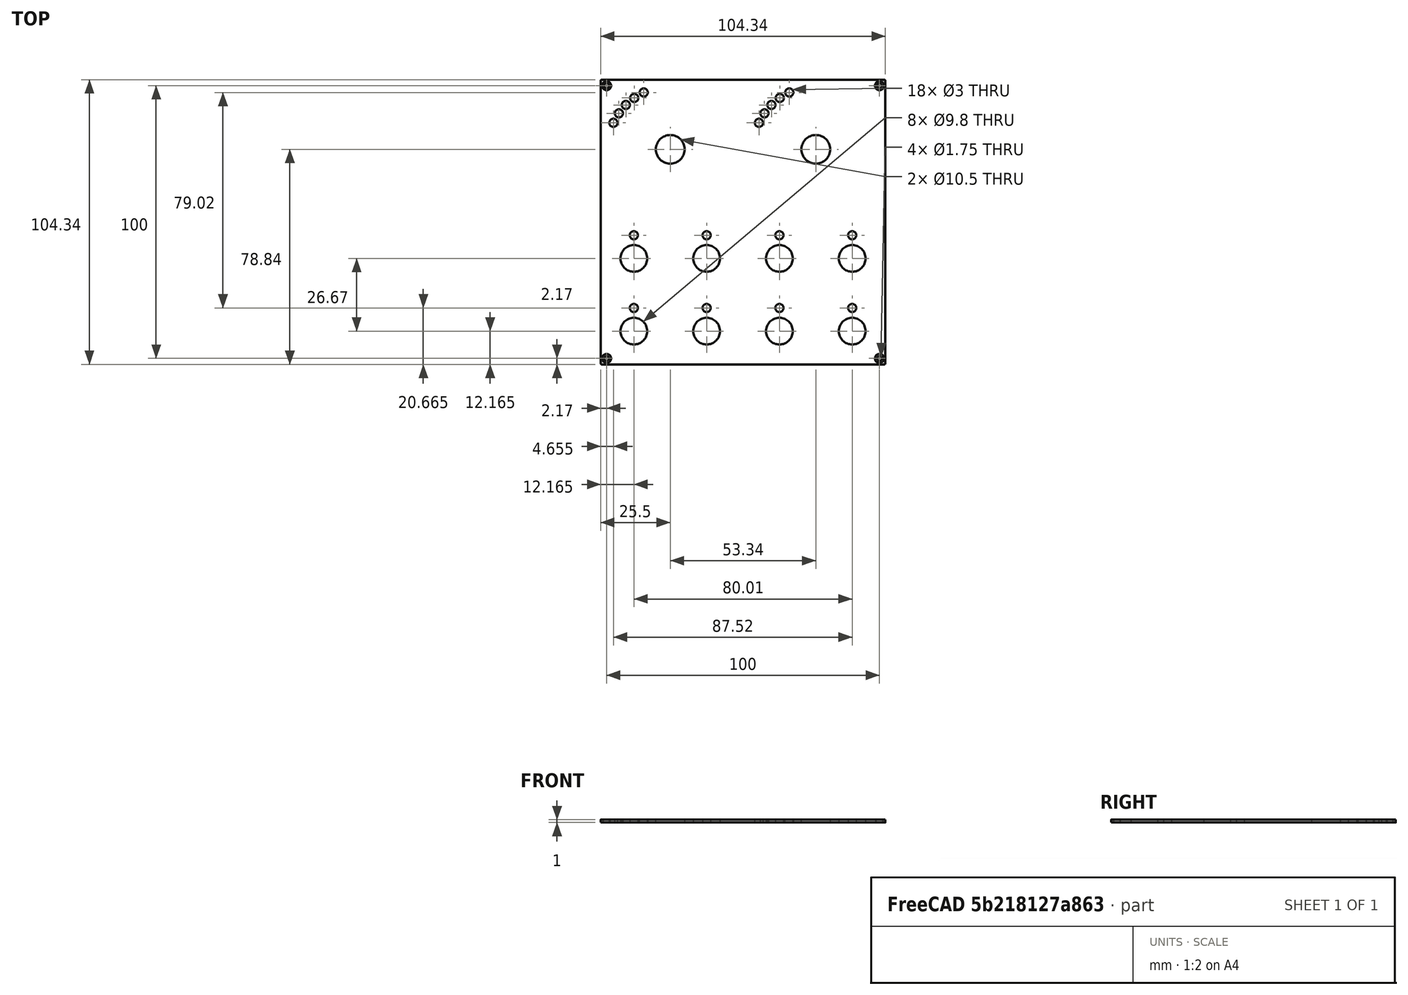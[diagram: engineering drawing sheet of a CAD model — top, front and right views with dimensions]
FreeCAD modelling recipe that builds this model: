
FCSTD DOCUMENT  (FreeCAD 0.21R33771 (Git))
Label: FRONTPANEL-SHEET-TEK2
License: All rights reserved
LicenseURL: https://en.wikipedia.org/wiki/All_rights_reserved
objects: TechDraw::DrawViewBalloon×16, TechDraw::DrawViewDimension×11, Sketcher::SketchObject×7, TechDraw::DrawViewPart×5, TechDraw::DrawHatch×5, PartDesign::Hole×3, TechDraw::DrawViewAnnotation×3, TechDraw::DrawSVGTemplate×2, PartDesign::Pocket×2, PartDesign::Body×2, TechDraw::DrawPage×2, Spreadsheet::Sheet×1, PartDesign::Pad×1, PartDesign::FeatureBase×1, TechDraw::DrawComplexSection×1
note: 37 computed .brp shape members not serialized (recipe doc carries the construction recipe); baked Part::Feature solids carry a one-line shape summary decoded from their .brp

FEATURE [TechDraw::DrawSVGTemplate] Template
  EditableTexts = COLOR=Anodized matte black - RAL code: 9004; CreationDate=2024/05/14; E.G.APPROVED=APPROVED; FC-Scale=1:1; FC-Title=TEK2 - frontpanel; IntechStudioLtd.=Intech Studio Ltd.; MATERIAL=Aluminum 5052-H32; REV=03; STANDARD=ISO 2768 - m
  Height = 297
  Orientation = 1
  Template = <userpath>/Desktop/A3_LandscapeTD_MODIFIED.svg
  Width = 420
FEATURE [Spreadsheet::Sheet] Spreadsheet  label="dim"
  cells = A1='panel_length; B1(panel_length)=104.35; A2='panel_thickness; B2(panel_thickness)=1; A3='panel_radius; B3(panel_radius)==(104.35 - 103.6) / 2; A5='corner_drill_dist; B5(corner_drill_dist)=100; A6='corner_drill_dia; B6(corner_drill_dia)=1.75; A7='corner_drill_countersink; B7(corner_drill_countersink)=3.3; A9='undercut_width; B9(undercut_width)=1; A10='undercut_length; B10(undercut_length)=90; A11='undercut_offset; B11(undercut_offset)=1; A12='undercut_depth; B12(undercut_depth)=0.8; A14='ui_raster; B14(ui_raster)=26.67; A16='light_drill_dia; B16(light_drill_dia)=3; D16='old 2.9; A17='light_bore_dia; B17(light_bore_dia)=3.45; C17='check; D17='old 3.30; E17='DEPRICATED; A18='light_bore_depth; B18(light_bore_depth)=0.4; C18='check; D18='old 0.40; E18='DEPRICATED; A20='pot_drill_dia; B20(pot_drill_dia)=9.8; C20='check; D20='old 6.20; A21='pot_led_dist; B21(pot_led_dist)=8.5; B22=0; A23='but_drill_dia; B23(but_drill_dia)=9.8; A24='but_led_dist; B24(but_led_dist)=8.5; A26='fad_cutout_width; B26(fad_cutout_width)=2.1; C26='check; D26='old 1.50; A27='fad_cutout_length; B27(fad_cutout_length)=36; A28='fad_led_dist; B28(fad_led_dist)=25; A30='enc_drill_dia; B30(enc_drill_dia)=9.8; C30='check; D30='old 6.20; A31='enc_led_dist; B31(enc_led_dist)=8.5; A33='longfad_cutout_width; B33(longfad_cutout_width)=2.1; A34='longfad_cutout_length; B34(longfad_cutout_length)=66; A36='panel_chamfer; B36(panel_chamfer)=0.2; C36='UPDATE DRAWING
FEATURE [Sketcher::SketchObject] Sketch025
  FullyConstrained = true
  MapMode = 5
  Support = -> [XY_Plane011]
  expr: Constraints[49] = <<dim>>.light_drill_dia
  sketch-geometry (28):
    g0: Circle CenterX=-26.67 CenterY=26.67 CenterZ=0 NormalX=0 NormalY=0 NormalZ=1 AngleXU=0 Radius=5.25
    g1: Circle CenterX=26.67 CenterY=26.67 CenterZ=0 NormalX=0 NormalY=0 NormalZ=1 AngleXU=0 Radius=5.25
    g2: LineSegment StartX=-26.67 StartY=26.67 StartZ=0 EndX=0 EndY=26.67 EndZ=0
    g3: LineSegment StartX=0 StartY=26.67 StartZ=0 EndX=0 EndY=0 EndZ=0
    g4: LineSegment StartX=26.67 StartY=26.67 StartZ=0 EndX=0 EndY=26.67 EndZ=0
    g5: Circle CenterX=-26.67 CenterY=26.67 CenterZ=0 NormalX=0 NormalY=0 NormalZ=1 AngleXU=0 Radius=23
    g6: Circle CenterX=26.67 CenterY=26.67 CenterZ=0 NormalX=0 NormalY=0 NormalZ=1 AngleXU=0 Radius=23
    g7: Circle CenterX=-47.5151 CenterY=36.3902 CenterZ=0 NormalX=0 NormalY=0 NormalZ=1 AngleXU=0 Radius=1.5
    g8: Circle CenterX=-45.5105 CenterY=39.8623 CenterZ=0 NormalX=0 NormalY=0 NormalZ=1 AngleXU=0 Radius=1.5
    g9: Circle CenterX=-42.9335 CenterY=42.9335 CenterZ=0 NormalX=0 NormalY=0 NormalZ=1 AngleXU=0 Radius=1.5
    g10: Circle CenterX=-39.8623 CenterY=45.5105 CenterZ=0 NormalX=0 NormalY=0 NormalZ=1 AngleXU=0 Radius=1.5
    g11: Circle CenterX=-36.3902 CenterY=47.5151 CenterZ=0 NormalX=0 NormalY=0 NormalZ=1 AngleXU=0 Radius=1.5
    g12: Circle CenterX=5.82492 CenterY=36.3902 CenterZ=0 NormalX=0 NormalY=0 NormalZ=1 AngleXU=0 Radius=1.5
    g13: Circle CenterX=7.8295 CenterY=39.8623 CenterZ=0 NormalX=0 NormalY=0 NormalZ=1 AngleXU=0 Radius=1.5
    g14: Circle CenterX=10.4065 CenterY=42.9335 CenterZ=0 NormalX=0 NormalY=0 NormalZ=1 AngleXU=0 Radius=1.5
    g15: Circle CenterX=13.4777 CenterY=45.5105 CenterZ=0 NormalX=0 NormalY=0 NormalZ=1 AngleXU=0 Radius=1.5
    g16: Circle CenterX=16.9498 CenterY=47.5151 CenterZ=0 NormalX=0 NormalY=0 NormalZ=1 AngleXU=0 Radius=1.5
    g17: LineSegment StartX=-47.5151 StartY=36.3902 StartZ=0 EndX=5.82492 EndY=36.3902 EndZ=0
    g18: LineSegment StartX=-45.5105 StartY=39.8623 StartZ=0 EndX=7.8295 EndY=39.8623 EndZ=0
    g19: LineSegment StartX=-42.9335 StartY=42.9335 StartZ=0 EndX=10.4065 EndY=42.9335 EndZ=0
    g20: LineSegment StartX=-39.8623 StartY=45.5105 StartZ=0 EndX=13.4777 EndY=45.5105 EndZ=0
    g21: LineSegment StartX=-36.3902 StartY=47.5151 StartZ=0 EndX=16.9498 EndY=47.5151 EndZ=0
    g22: LineSegment StartX=5.82492 StartY=36.3902 StartZ=0 EndX=26.67 EndY=26.67 EndZ=0
    g23: LineSegment StartX=16.9498 StartY=47.5151 StartZ=0 EndX=26.67 EndY=26.67 EndZ=0
    g24: LineSegment StartX=5.82492 StartY=36.3902 StartZ=0 EndX=7.8295 EndY=39.8623 EndZ=0
    g25: LineSegment StartX=7.8295 StartY=39.8623 StartZ=0 EndX=10.4065 EndY=42.9335 EndZ=0
    g26: LineSegment StartX=13.4777 StartY=45.5105 StartZ=0 EndX=10.4065 EndY=42.9335 EndZ=0
    g27: LineSegment StartX=16.9498 StartY=47.5151 StartZ=0 EndX=13.4777 EndY=45.5105 EndZ=0
  constraints (69):
    c: Coincident(g2,g0)
    c: PointOnObject(g2,g-2)
    c: Coincident(g2,g3)
    c: Coincident(g3,g-1)
    c: Coincident(g4,g1)
    c: Coincident(g4,g2)
    c: Equal(g3,g2)
    c: Equal(g2,g4)
    c: Horizontal(g2)
    c: Horizontal(g4)
    c: DistanceY(g3,g3) = 26.67
    c: Equal(g0,g1)
    c: Coincident(g5,g0)
    c: Coincident(g6,g1)
    c: Equal(g6,g5)
    c: PointOnObject(g7,g5)
    c: PointOnObject(g8,g5)
    c: PointOnObject(g9,g5)
    c: PointOnObject(g10,g5)
    c: PointOnObject(g11,g5)
    c: PointOnObject(g12,g6)
    c: PointOnObject(g13,g6)
    c: PointOnObject(g14,g6)
    c: PointOnObject(g15,g6)
    c: PointOnObject(g16,g6)
    c: Equal(g7,g8)
    c: Equal(g8,g9)
    c: Equal(g9,g10)
    c: Equal(g10,g11)
    c: Equal(g11,g12)
    c: Equal(g12,g13)
    c: Equal(g13,g14)
    c: Equal(g14,g15)
    c: Equal(g15,g16)
    c: Coincident(g17,g7)
    c: Coincident(g17,g12)
    c: Coincident(g18,g8)
    c: Coincident(g18,g13)
    c: Horizontal(g18)
    c: Coincident(g19,g9)
    c: Coincident(g19,g14)
    c: Horizontal(g19)
    c: Coincident(g20,g10)
    c: Coincident(g20,g15)
    c: Horizontal(g20)
    c: Coincident(g21,g11)
    c: Horizontal(g21)
    c: Coincident(g21,g16)
    c: Horizontal(g17)
    c: Diameter(g12) = 3
    c: Coincident(g22,g12)
    c: Coincident(g22,g1)
    c: Coincident(g23,g16)
    c: Coincident(g23,g1)
    c: Angle(g22,g4) = 0.436332
    c: Angle(g-2,g23) = 0.436332
    c: Coincident(g24,g12)
    c: Coincident(g24,g13)
    c: Coincident(g25,g13)
    c: Coincident(g26,g15)
    c: Coincident(g26,g25)
    c: Coincident(g27,g16)
    c: Coincident(g27,g15)
    c: Coincident(g25,g14)
    c: Equal(g24,g25)
    c: Equal(g25,g26)
    c: Equal(g26,g27)
    c: Radius(g6) = 23
    c: Diameter(g1) = 10.5
FEATURE [Sketcher::SketchObject] Sketch024
  FullyConstrained = true
  MapMode = 5
  Support = -> [XY_Plane011]
  expr: Constraints[42] = <<dim>>.but_led_dist
  sketch-geometry (17):
    g0: Circle CenterX=-40.005 CenterY=-4.835 CenterZ=0 NormalX=0 NormalY=0 NormalZ=1 AngleXU=0 Radius=2
    g1: Circle CenterX=-13.335 CenterY=-4.835 CenterZ=0 NormalX=0 NormalY=0 NormalZ=1 AngleXU=0 Radius=2
    g2: LineSegment StartX=-40.005 StartY=-4.835 StartZ=0 EndX=-13.335 EndY=-4.835 EndZ=0
    g3: Circle CenterX=13.335 CenterY=-4.835 CenterZ=0 NormalX=0 NormalY=0 NormalZ=1 AngleXU=0 Radius=2
    g4: LineSegment StartX=-13.335 StartY=-4.835 StartZ=0 EndX=13.335 EndY=-4.835 EndZ=0
    g5: Circle CenterX=40.005 CenterY=-4.835 CenterZ=0 NormalX=0 NormalY=0 NormalZ=1 AngleXU=0 Radius=2
    g6: LineSegment StartX=13.335 StartY=-4.835 StartZ=0 EndX=40.005 EndY=-4.835 EndZ=0
    g7: Circle CenterX=-40.005 CenterY=-31.505 CenterZ=0 NormalX=0 NormalY=0 NormalZ=1 AngleXU=0 Radius=2
    g8: LineSegment StartX=-40.005 StartY=-4.835 StartZ=0 EndX=-40.005 EndY=-31.505 EndZ=0
    g9: Circle CenterX=-13.335 CenterY=-31.505 CenterZ=0 NormalX=0 NormalY=0 NormalZ=1 AngleXU=0 Radius=2
    g10: LineSegment StartX=-40.005 StartY=-31.505 StartZ=0 EndX=-13.335 EndY=-31.505 EndZ=0
    g11: Circle CenterX=13.335 CenterY=-31.505 CenterZ=0 NormalX=0 NormalY=0 NormalZ=1 AngleXU=0 Radius=2
    g12: LineSegment StartX=-13.335 StartY=-31.505 StartZ=0 EndX=13.335 EndY=-31.505 EndZ=0
    g13: Circle CenterX=40.005 CenterY=-31.505 CenterZ=0 NormalX=0 NormalY=0 NormalZ=1 AngleXU=0 Radius=2
    g14: LineSegment StartX=13.335 StartY=-31.505 StartZ=0 EndX=40.005 EndY=-31.505 EndZ=0
    g15: LineSegment StartX=-13.335 StartY=-4.835 StartZ=0 EndX=-1.8e-15 EndY=8.5 EndZ=0
    g16: LineSegment StartX=-1.8e-15 StartY=8.5 StartZ=0 EndX=13.335 EndY=-4.835 EndZ=0
  constraints (43):
    c: Diameter(g0) = 4
    c: Coincident(g0,g2)
    c: Coincident(g1,g2)
    c: Coincident(g1,g4)
    c: Coincident(g3,g4)
    c: Coincident(g3,g6)
    c: Coincident(g5,g6)
    c: Coincident(g0,g8)
    c: Coincident(g7,g8)
    c: Coincident(g7,g10)
    c: Coincident(g9,g10)
    c: Coincident(g9,g12)
    c: Coincident(g11,g12)
    c: Coincident(g11,g14)
    c: Coincident(g13,g14)
    c: Horizontal(g4)
    c: Horizontal(g2)
    c: Horizontal(g6)
    c: Horizontal(g10)
    c: Horizontal(g12)
    c: Horizontal(g14)
    c: Vertical(g8)
    c: Equal(g8,g2)
    c: Equal(g2,g10)
    c: Equal(g10,g12)
    c: Equal(g12,g4)
    c: Equal(g4,g6)
    c: Equal(g6,g14)
    c: DistanceX(g4,g4) = 26.67
    c: Equal(g7,g9)
    c: Equal(g9,g11)
    c: Equal(g11,g13)
    c: Equal(g13,g5)
    c: Equal(g5,g3)
    c: Equal(g3,g1)
    c: Equal(g1,g0)
    c: Coincident(g15,g1)
    c: PointOnObject(g15,g-2)
    c: Coincident(g15,g16)
    c: Coincident(g16,g3)
    c: Equal(g16,g15)
    c: Perpendicular(g15,g16)
    c: DistanceY(g-1,g15) = 8.5
FEATURE [Sketcher::SketchObject] Sketch023
  FullyConstrained = true
  MapMode = 5
  Support = -> [XY_Plane011]
  sketch-geometry (17):
    g0: Circle CenterX=-40.005 CenterY=-13.335 CenterZ=0 NormalX=0 NormalY=0 NormalZ=1 AngleXU=0 Radius=2
    g1: Circle CenterX=-13.335 CenterY=-13.335 CenterZ=0 NormalX=0 NormalY=0 NormalZ=1 AngleXU=0 Radius=2
    g2: LineSegment StartX=-40.005 StartY=-13.335 StartZ=0 EndX=-13.335 EndY=-13.335 EndZ=0
    g3: Circle CenterX=13.335 CenterY=-13.335 CenterZ=0 NormalX=0 NormalY=0 NormalZ=1 AngleXU=0 Radius=2
    g4: LineSegment StartX=-13.335 StartY=-13.335 StartZ=0 EndX=13.335 EndY=-13.335 EndZ=0
    g5: Circle CenterX=40.005 CenterY=-13.335 CenterZ=0 NormalX=0 NormalY=0 NormalZ=1 AngleXU=0 Radius=2
    g6: LineSegment StartX=13.335 StartY=-13.335 StartZ=0 EndX=40.005 EndY=-13.335 EndZ=0
    g7: Circle CenterX=-40.005 CenterY=-40.005 CenterZ=0 NormalX=0 NormalY=0 NormalZ=1 AngleXU=0 Radius=2
    g8: LineSegment StartX=-40.005 StartY=-13.335 StartZ=0 EndX=-40.005 EndY=-40.005 EndZ=0
    g9: Circle CenterX=-13.335 CenterY=-40.005 CenterZ=0 NormalX=0 NormalY=0 NormalZ=1 AngleXU=0 Radius=2
    g10: LineSegment StartX=-40.005 StartY=-40.005 StartZ=0 EndX=-13.335 EndY=-40.005 EndZ=0
    g11: Circle CenterX=13.335 CenterY=-40.005 CenterZ=0 NormalX=0 NormalY=0 NormalZ=1 AngleXU=0 Radius=2
    g12: LineSegment StartX=-13.335 StartY=-40.005 StartZ=0 EndX=13.335 EndY=-40.005 EndZ=0
    g13: Circle CenterX=40.005 CenterY=-40.005 CenterZ=0 NormalX=0 NormalY=0 NormalZ=1 AngleXU=0 Radius=2
    g14: LineSegment StartX=13.335 StartY=-40.005 StartZ=0 EndX=40.005 EndY=-40.005 EndZ=0
    g15: LineSegment StartX=0 StartY=0 StartZ=0 EndX=13.335 EndY=-13.335 EndZ=0
    g16: LineSegment StartX=0 StartY=0 StartZ=0 EndX=-13.335 EndY=-13.335 EndZ=0
  constraints (42):
    c: Diameter(g0) = 4
    c: Coincident(g0,g2)
    c: Coincident(g1,g2)
    c: Coincident(g1,g4)
    c: Coincident(g3,g4)
    c: Coincident(g3,g6)
    c: Coincident(g5,g6)
    c: Coincident(g0,g8)
    c: Coincident(g7,g8)
    c: Coincident(g7,g10)
    c: Coincident(g9,g10)
    c: Coincident(g9,g12)
    c: Coincident(g11,g12)
    c: Coincident(g11,g14)
    c: Coincident(g13,g14)
    c: Coincident(g-1,g16)
    c: Coincident(g16,g1)
    c: Coincident(g15,g3)
    c: Horizontal(g4)
    c: Horizontal(g2)
    c: Horizontal(g6)
    c: Horizontal(g10)
    c: Horizontal(g12)
    c: Horizontal(g14)
    c: Vertical(g8)
    c: Equal(g8,g2)
    c: Equal(g2,g10)
    c: Equal(g10,g12)
    c: Equal(g12,g4)
    c: Equal(g4,g6)
    c: Equal(g6,g14)
    c: DistanceX(g4,g4) = 26.67
    c: Equal(g16,g15)
    c: Coincident(g15,g16)
    c: Perpendicular(g15,g16)
    c: Equal(g7,g9)
    c: Equal(g9,g11)
    c: Equal(g11,g13)
    c: Equal(g13,g5)
    c: Equal(g5,g3)
    c: Equal(g3,g1)
    c: Equal(g1,g0)
FEATURE [Sketcher::SketchObject] Sketch001
  FullyConstrained = true
  MapMode = 5
  Support = -> [XY_Plane]
  expr: Constraints[13] = <<dim>>.corner_drill_dist
  sketch-geometry (9):
    g0: LineSegment StartX=-50 StartY=50 StartZ=0 EndX=-50 EndY=-50 EndZ=0
    g1: LineSegment StartX=-50 StartY=-50 StartZ=0 EndX=50 EndY=-50 EndZ=0
    g2: LineSegment StartX=50 StartY=-50 StartZ=0 EndX=50 EndY=50 EndZ=0
    g3: LineSegment StartX=50 StartY=50 StartZ=0 EndX=-50 EndY=50 EndZ=0
    g4: Circle CenterX=0 CenterY=0 CenterZ=0 NormalX=0 NormalY=0 NormalZ=1 AngleXU=0 Radius=70.7107
    g5: Circle CenterX=-50 CenterY=50 CenterZ=0 NormalX=0 NormalY=0 NormalZ=1 AngleXU=0 Radius=0.5
    g6: Circle CenterX=50 CenterY=50 CenterZ=0 NormalX=0 NormalY=0 NormalZ=1 AngleXU=0 Radius=0.5
    g7: Circle CenterX=50 CenterY=-50 CenterZ=0 NormalX=0 NormalY=0 NormalZ=1 AngleXU=0 Radius=0.5
    g8: Circle CenterX=-50 CenterY=-50 CenterZ=0 NormalX=0 NormalY=0 NormalZ=1 AngleXU=0 Radius=0.5
  constraints (22):
    c: Coincident(g0,g1)
    c: Coincident(g1,g2)
    c: Coincident(g2,g3)
    c: Coincident(g3,g0)
    c: Equal(g0,g1)
    c: Equal(g0,g2)
    c: Equal(g0,g3)
    c: PointOnObject(g0,g4)
    c: PointOnObject(g1,g4)
    c: PointOnObject(g2,g4)
    c: PointOnObject(g3,g4)
    c: Coincident(g4,g-1)
    c: Horizontal(g3)
    c: DistanceX(g3,g3) = 100
    c: Coincident(g5,g0)
    c: Coincident(g6,g2)
    c: Coincident(g7,g1)
    c: Coincident(g8,g0)
    c: Diameter(g8) = 1
    c: Equal(g8,g7)
    c: Equal(g8,g6)
    c: Equal(g8,g5)
FEATURE [Sketcher::SketchObject] Sketch002
  AttachmentOffset = pos=(0,0,-4.8) rot=(0,0,1;0rad)
  FullyConstrained = true
  MapMode = 5
  Placement = pos=(0,0,-4.8) rot=(0,0,1;0rad)
  Support = -> [XY_Plane]
  expr: .AttachmentOffset.Base.z = -<<dim>>.undercut_depth - 4
  expr: Constraints[91] = <<dim>>.undercut_length
  expr: Constraints[92] = <<dim>>.undercut_width
  expr: Constraints[93] = <<dim>>.panel_length / 2 - <<dim>>.undercut_offset - <<dim>>.undercut_width / 2
  sketch-geometry (40):
    g0: LineSegment StartX=-45 StartY=50.175 StartZ=0 EndX=45 EndY=50.175 EndZ=0
    g1: LineSegment StartX=-45 StartY=51.175 StartZ=0 EndX=45 EndY=51.175 EndZ=0
    g2: LineSegment StartX=-50.675 StartY=45 StartZ=0 EndX=0 EndY=0 EndZ=0
    g3: LineSegment StartX=0 StartY=0 StartZ=0 EndX=-50.675 EndY=-45 EndZ=0
    g4: LineSegment StartX=0 StartY=0 StartZ=0 EndX=-45 EndY=50.675 EndZ=0
    g5: LineSegment StartX=45 StartY=50.675 StartZ=0 EndX=0 EndY=0 EndZ=0
    g6: LineSegment StartX=0 StartY=0 StartZ=0 EndX=50.675 EndY=45 EndZ=0
    g7: LineSegment StartX=50.675 StartY=-45 StartZ=0 EndX=0 EndY=0 EndZ=0
    g8: LineSegment StartX=0 StartY=0 StartZ=0 EndX=45 EndY=-50.675 EndZ=0
    g9: LineSegment StartX=0 StartY=0 StartZ=0 EndX=-45 EndY=-50.675 EndZ=0
    g10: ArcOfCircle CenterX=45 CenterY=50.675 CenterZ=0 NormalX=0 NormalY=0 NormalZ=1 AngleXU=0 Radius=0.5 StartAngle=4.71239 EndAngle=6.28319
    g11: ArcOfCircle CenterX=45 CenterY=50.675 CenterZ=0 NormalX=0 NormalY=0 NormalZ=1 AngleXU=0 Radius=0.5 StartAngle=0 EndAngle=1.5708
    g12: LineSegment StartX=45 StartY=50.675 StartZ=0 EndX=45.5 EndY=50.675 EndZ=0
    g13: ArcOfCircle CenterX=-45 CenterY=50.675 CenterZ=0 NormalX=0 NormalY=0 NormalZ=1 AngleXU=0 Radius=0.5 StartAngle=3.14159 EndAngle=4.71239
    g14: ArcOfCircle CenterX=-45 CenterY=50.675 CenterZ=0 NormalX=0 NormalY=0 NormalZ=1 AngleXU=0 Radius=0.5 StartAngle=1.5708 EndAngle=3.14159
    g15: LineSegment StartX=-45.5 StartY=50.675 StartZ=0 EndX=-45 EndY=50.675 EndZ=0
    g16: LineSegment StartX=-45 StartY=-51.175 StartZ=0 EndX=45 EndY=-51.175 EndZ=0
    g17: LineSegment StartX=-45 StartY=-50.175 StartZ=0 EndX=45 EndY=-50.175 EndZ=0
    g18: ArcOfCircle CenterX=45 CenterY=-50.675 CenterZ=0 NormalX=0 NormalY=0 NormalZ=1 AngleXU=0 Radius=0.5 StartAngle=4.71239 EndAngle=6.28319
    g19: ArcOfCircle CenterX=45 CenterY=-50.675 CenterZ=0 NormalX=0 NormalY=0 NormalZ=1 AngleXU=0 Radius=0.5 StartAngle=0 EndAngle=1.5708
    g20: LineSegment StartX=45 StartY=-50.675 StartZ=0 EndX=45.5 EndY=-50.675 EndZ=0
    g21: ArcOfCircle CenterX=-45 CenterY=-50.675 CenterZ=0 NormalX=0 NormalY=0 NormalZ=1 AngleXU=0 Radius=0.5 StartAngle=3.14159 EndAngle=4.71239
    g22: ArcOfCircle CenterX=-45 CenterY=-50.675 CenterZ=0 NormalX=0 NormalY=0 NormalZ=1 AngleXU=0 Radius=0.5 StartAngle=1.5708 EndAngle=3.14159
    g23: LineSegment StartX=-45.5 StartY=-50.675 StartZ=0 EndX=-45 EndY=-50.675 EndZ=0
    g24: LineSegment StartX=51.175 StartY=-45 StartZ=0 EndX=51.175 EndY=45 EndZ=0
    g25: LineSegment StartX=50.175 StartY=-45 StartZ=0 EndX=50.175 EndY=45 EndZ=0
    g26: ArcOfCircle CenterX=50.675 CenterY=45 CenterZ=0 NormalX=0 NormalY=0 NormalZ=1 AngleXU=0 Radius=0.5 StartAngle=3.8e-15 EndAngle=1.5708
    g27: ArcOfCircle CenterX=50.675 CenterY=45 CenterZ=0 NormalX=0 NormalY=0 NormalZ=1 AngleXU=0 Radius=0.5 StartAngle=1.5708 EndAngle=3.14159
    g28: LineSegment StartX=50.675 StartY=45 StartZ=0 EndX=50.675 EndY=45.5 EndZ=0
    g29: ArcOfCircle CenterX=50.675 CenterY=-45 CenterZ=0 NormalX=0 NormalY=0 NormalZ=1 AngleXU=0 Radius=0.5 StartAngle=4.71239 EndAngle=6.28319
    g30: ArcOfCircle CenterX=50.675 CenterY=-45 CenterZ=0 NormalX=0 NormalY=0 NormalZ=1 AngleXU=0 Radius=0.5 StartAngle=3.14159 EndAngle=4.71239
    g31: LineSegment StartX=50.675 StartY=-45.5 StartZ=0 EndX=50.675 EndY=-45 EndZ=0
    g32: LineSegment StartX=-50.175 StartY=-45 StartZ=0 EndX=-50.175 EndY=45 EndZ=0
    g33: LineSegment StartX=-51.175 StartY=-45 StartZ=0 EndX=-51.175 EndY=45 EndZ=0
    g34: ArcOfCircle CenterX=-50.675 CenterY=45 CenterZ=0 NormalX=0 NormalY=0 NormalZ=1 AngleXU=0 Radius=0.5 StartAngle=1.4e-15 EndAngle=1.5708
    g35: ArcOfCircle CenterX=-50.675 CenterY=45 CenterZ=0 NormalX=0 NormalY=0 NormalZ=1 AngleXU=0 Radius=0.5 StartAngle=1.5708 EndAngle=3.14159
    g36: LineSegment StartX=-50.675 StartY=45 StartZ=0 EndX=-50.675 EndY=45.5 EndZ=0
    g37: ArcOfCircle CenterX=-50.675 CenterY=-45 CenterZ=0 NormalX=0 NormalY=0 NormalZ=1 AngleXU=0 Radius=0.5 StartAngle=4.71239 EndAngle=6.28319
    g38: ArcOfCircle CenterX=-50.675 CenterY=-45 CenterZ=0 NormalX=0 NormalY=0 NormalZ=1 AngleXU=0 Radius=0.5 StartAngle=3.14159 EndAngle=4.71239
    g39: LineSegment StartX=-50.675 StartY=-45.5 StartZ=0 EndX=-50.675 EndY=-45 EndZ=0
  constraints (96):
    c: Horizontal(g0)
    c: Coincident(g2,g-1)
    c: Coincident(g2,g3)
    c: Coincident(g-1,g4)
    c: Coincident(g5,g-1)
    c: Coincident(g5,g6)
    c: Coincident(g7,g-1)
    c: Coincident(g7,g8)
    c: Coincident(g-1,g9)
    c: Equal(g5,g6)
    c: Equal(g6,g8)
    c: Equal(g8,g7)
    c: Equal(g7,g9)
    c: Equal(g9,g3)
    c: Equal(g3,g2)
    c: Equal(g2,g4)
    c: Coincident(g10,g5)
    c: Coincident(g11,g10)
    c: Coincident(g11,g10)
    c: Tangent(g11,g1) = 1.5708
    c: Tangent(g10,g0) = -1.5708
    c: Coincident(g12,g10)
    c: Coincident(g12,g10)
    c: Horizontal(g12)
    c: Coincident(g13,g4)
    c: Coincident(g14,g13)
    c: Coincident(g14,g13)
    c: Tangent(g14,g1) = 1.5708
    c: Tangent(g13,g0) = -1.5708
    c: Coincident(g15,g13)
    c: Coincident(g15,g13)
    c: Horizontal(g15)
    c: Horizontal(g1)
    c: Horizontal(g16)
    c: Coincident(g19,g18)
    c: Coincident(g19,g18)
    c: Tangent(g19,g17) = 1.5708
    c: Tangent(g18,g16) = -1.5708
    c: Coincident(g20,g18)
    c: Coincident(g20,g18)
    c: Horizontal(g20)
    c: Coincident(g22,g21)
    c: Coincident(g22,g21)
    c: Tangent(g22,g17) = 1.5708
    c: Tangent(g21,g16) = -1.5708
    c: Coincident(g23,g21)
    c: Coincident(g23,g21)
    c: Horizontal(g23)
    c: Horizontal(g17)
    c: Coincident(g21,g9)
    c: Coincident(g8,g18)
    c: Equal(g22,g14)
    c: Equal(g17,g1)
    c: Coincident(g27,g26)
    c: Coincident(g27,g26)
    c: Tangent(g27,g25) = 1.5708
    c: Tangent(g26,g24) = -1.5708
    c: Coincident(g28,g26)
    c: Coincident(g28,g26)
    c: Coincident(g30,g29)
    c: Coincident(g30,g29)
    c: Tangent(g30,g25) = 1.5708
    c: Tangent(g29,g24) = -1.5708
    c: Coincident(g31,g29)
    c: Coincident(g31,g29)
    c: Vertical(g31)
    c: Vertical(g28)
    c: Vertical(g25)
    c: Vertical(g24)
    c: Coincident(g35,g34)
    c: Coincident(g35,g34)
    c: Tangent(g35,g33) = 1.5708
    c: Tangent(g34,g32) = -1.5708
    c: Coincident(g36,g34)
    c: Coincident(g36,g34)
    c: Coincident(g38,g37)
    c: Coincident(g38,g37)
    c: Tangent(g38,g33) = 1.5708
    c: Tangent(g37,g32) = -1.5708
    c: Coincident(g39,g37)
    c: Coincident(g39,g37)
    c: Vertical(g39)
    c: Vertical(g36)
    c: Vertical(g33)
    c: Vertical(g32)
    c: Coincident(g6,g26)
    c: Coincident(g7,g29)
    c: Equal(g25,g0)
    c: Equal(g11,g27)
    c: Equal(g1,g33)
    c: Equal(g35,g11)
    c: DistanceX(g13,g10) = 90
    c: Diameter(g13) = 1
    c: DistanceY(g-1,g13) = 50.675
    c: Coincident(g2,g34)
    c: Coincident(g3,g37)
FEATURE [Sketcher::SketchObject] Sketch
  FullyConstrained = true
  MapMode = 5
  Support = -> [XY_Plane]
  expr: Constraints[12] = <<dim>>.panel_radius
  expr: Constraints[16] = <<dim>>.panel_length
  sketch-geometry (11):
    g0: LineSegment StartX=-51.8 StartY=52.175 StartZ=0 EndX=51.8 EndY=52.175 EndZ=0
    g1: LineSegment StartX=52.175 StartY=51.8 StartZ=0 EndX=52.175 EndY=-51.8 EndZ=0
    g2: LineSegment StartX=51.8 StartY=-52.175 StartZ=0 EndX=-51.8 EndY=-52.175 EndZ=0
    g3: LineSegment StartX=-52.175 StartY=-51.8 StartZ=0 EndX=-52.175 EndY=51.8 EndZ=0
    g4: ArcOfCircle CenterX=-51.8 CenterY=51.8 CenterZ=0 NormalX=0 NormalY=0 NormalZ=1 AngleXU=0 Radius=0.375 StartAngle=1.5708 EndAngle=3.14159
    g5: ArcOfCircle CenterX=51.8 CenterY=51.8 CenterZ=0 NormalX=0 NormalY=0 NormalZ=1 AngleXU=0 Radius=0.375 StartAngle=8.4e-15 EndAngle=1.5708
    g6: ArcOfCircle CenterX=51.8 CenterY=-51.8 CenterZ=0 NormalX=0 NormalY=0 NormalZ=1 AngleXU=0 Radius=0.375 StartAngle=4.71239 EndAngle=6.28319
    g7: ArcOfCircle CenterX=-51.8 CenterY=-51.8 CenterZ=0 NormalX=0 NormalY=0 NormalZ=1 AngleXU=0 Radius=0.375 StartAngle=3.14159 EndAngle=4.71239
    g8: LineSegment StartX=-51.8 StartY=51.8 StartZ=0 EndX=0 EndY=0 EndZ=0
    g9: LineSegment StartX=0 StartY=0 StartZ=0 EndX=51.8 EndY=51.8 EndZ=0
    g10: LineSegment StartX=0 StartY=0 StartZ=0 EndX=-51.8 EndY=-51.8 EndZ=0
  constraints (26):
    c: Horizontal(g0)
    c: Horizontal(g2)
    c: Vertical(g1)
    c: Vertical(g3)
    c: Tangent(g3,g4) = 1.5708
    c: Tangent(g0,g4) = 1.5708
    c: Tangent(g0,g5) = 1.5708
    c: Tangent(g1,g5) = 1.5708
    c: Tangent(g1,g6) = 1.5708
    c: Tangent(g2,g6) = 1.5708
    c: Tangent(g2,g7) = 1.5708
    c: Tangent(g3,g7) = 1.5708
    c: Radius(g4) = 0.375
    c: Equal(g4,g5)
    c: Equal(g4,g6)
    c: Equal(g4,g7)
    c: DistanceX(g3,g1) = 104.35
    c: Equal(g3,g0)
    c: Coincident(g8,g4)
    c: Coincident(g8,g-1)
    c: Coincident(g8,g9)
    c: Coincident(g9,g5)
    c: Coincident(g-1,g10)
    c: Coincident(g10,g7)
    c: Equal(g10,g8)
    c: Equal(g8,g9)
FEATURE [PartDesign::Pad] Pad  label="panel"
  AllowMultiFace = false
  Direction = (0,0,1)
  Length = 1
  Length2 = 100
  Profile = -> Sketch
  Reversed = true
  Type = 0
  expr: Length = <<dim>>.panel_thickness
FEATURE [PartDesign::Pocket] Pocket
  AllowMultiFace = false
  BaseFeature = -> Pad
  Direction = (0,0,-1)
  Length = 5
  Length2 = 100
  Profile = -> Sketch002
  Type = 1
FEATURE [PartDesign::Hole] Hole
  BaseFeature = -> Pocket
  CustomThreadClearance = 0
  Depth = 298.105
  DepthType = 1
  Diameter = 1.75
  DrillForDepth = false
  DrillPoint = 1
  DrillPointAngle = 118
  HoleCutCountersinkAngle = 90
  HoleCutCustomValues = false
  HoleCutDepth = 0
  HoleCutDiameter = 3.3
  HoleCutType = 2
  ModelThread = false
  Profile = -> Sketch001
  Tapered = false
  TaperedAngle = 90
  ThreadClass = 0
  ThreadDepth = 298.105
  ThreadDepthType = 0
  ThreadDirection = 0
  ThreadFit = 0
  ThreadSize = 0
  ThreadType = 0
  Threaded = false
  UseCustomThreadClearance = false
  expr: Diameter = <<dim>>.corner_drill_dia
  expr: HoleCutDiameter = <<dim>>.corner_drill_countersink
FEATURE [PartDesign::Body] Body  label="Base"
  Group = -> [Sketch,Pad,Sketch001,Sketch002,Pocket,Hole]
  Origin = -> Origin
  Tip = -> Hole
FEATURE [PartDesign::FeatureBase] Clone009
  BaseFeature = -> Body
FEATURE [PartDesign::Hole] Hole014  label="TEK2_ButtonHole"
  BaseFeature = -> Clone009
  CustomThreadClearance = 0
  Depth = 25
  DepthType = 0
  Diameter = 9.8
  DrillForDepth = false
  DrillPoint = 1
  DrillPointAngle = 118
  HoleCutCountersinkAngle = 90
  HoleCutCustomValues = false
  HoleCutDepth = 0
  HoleCutDiameter = 6.1
  HoleCutType = 0
  ModelThread = false
  Profile = -> Sketch023
  Tapered = false
  TaperedAngle = 90
  ThreadClass = 0
  ThreadDepth = 25
  ThreadDepthType = 0
  ThreadDirection = 0
  ThreadFit = 0
  ThreadSize = 0
  ThreadType = 0
  Threaded = false
  UseCustomThreadClearance = false
  expr: Diameter = <<dim>>.but_drill_dia
FEATURE [PartDesign::Hole] Hole015  label="TEK2_ButtonLight"
  BaseFeature = -> Hole014
  CustomThreadClearance = 0
  Depth = 25
  DepthType = 0
  Diameter = 3
  DrillForDepth = false
  DrillPoint = 1
  DrillPointAngle = 118
  HoleCutCountersinkAngle = 90
  HoleCutCustomValues = false
  HoleCutDepth = 0
  HoleCutDiameter = 6.1
  HoleCutType = 0
  ModelThread = false
  Profile = -> Sketch024
  Tapered = false
  TaperedAngle = 90
  ThreadClass = 0
  ThreadDepth = 25
  ThreadDepthType = 0
  ThreadDirection = 0
  ThreadFit = 0
  ThreadSize = 0
  ThreadType = 0
  Threaded = false
  UseCustomThreadClearance = false
  expr: Diameter = <<dim>>.light_drill_dia
FEATURE [PartDesign::Pocket] Pocket007  label="TEK2_TEK_Light"
  BaseFeature = -> Hole015
  Direction = (0,0,-1)
  Length = 5
  Length2 = 5
  Profile = -> Sketch025
  ReferenceAxis = -> Sketch025 [N_Axis]
  Type = 0
FEATURE [Sketcher::SketchObject] Sketch026
  ExternalGeometry = -> [Pocket007]
  FullyConstrained = true
  MapMode = 5
  Support = -> [XY_Plane011]
  sketch-geometry (1):
    g0: LineSegment StartX=-53.5 StartY=-50 StartZ=0 EndX=-46.5 EndY=-50 EndZ=0
  constraints (3):
    c: Horizontal(g0)
    c: Symmetric(g0,g0,g-3)
    c: DistanceX(g0,g0) = 7
FEATURE [PartDesign::Body] Body011  label="FRONTPANEL-SHEET-TEK2"
  BaseFeature = -> Body
  Group = -> [Clone009,Sketch023,Sketch024,Hole014,Hole015,Sketch025,Pocket007,Sketch026]
  Origin = -> Origin011
  Tip = -> Pocket007
FEATURE [TechDraw::DrawViewPart] View
  CoarseView = false
  Direction = (0,0,1)
  Focus = 100
  HardHidden = true
  IsoCount = 0
  IsoHidden = false
  IsoVisible = false
  LockPosition = false
  Perspective = false
  Rotation = 0
  ScaleType = 0
  ScrubCount = 0
  SeamHidden = false
  SeamVisible = true
  SmoothHidden = false
  SmoothVisible = true
  Source = -> [Body011]
  X = 98.8745
  XDirection = (1,0,0)
  Y = 197.053
FEATURE [TechDraw::DrawViewPart] View001
  CoarseView = false
  Direction = (-1,0,0)
  Focus = 100
  HardHidden = true
  IsoCount = 0
  IsoHidden = false
  IsoVisible = false
  LockPosition = false
  Perspective = false
  Rotation = 0
  ScaleType = 0
  ScrubCount = 0
  SeamHidden = false
  SeamVisible = true
  SmoothHidden = false
  SmoothVisible = true
  Source = -> [Body011]
  X = 195.483
  XDirection = (0,0,1)
  Y = 199.908
FEATURE [TechDraw::DrawViewPart] View002
  CoarseView = false
  Direction = (0,0,-1)
  Focus = 100
  HardHidden = true
  IsoCount = 0
  IsoHidden = false
  IsoVisible = false
  LockPosition = false
  Perspective = false
  Rotation = 0
  ScaleType = 0
  ScrubCount = 0
  SeamHidden = false
  SeamVisible = true
  SmoothHidden = false
  SmoothVisible = true
  Source = -> [Body011]
  X = 288.076
  XDirection = (-1,0,0)
  Y = 198.167
FEATURE [TechDraw::DrawViewDimension] Dimension
  AngleOverride = false
  Arbitrary = false
  ArbitraryTolerances = false
  EqualTolerance = false
  ExtensionAngle = 0
  FormatSpec = %.2w
  FormatSpecOverTolerance = %+.2w
  FormatSpecUnderTolerance = %+.2w
  Inverted = false
  LineAngle = 0
  LockPosition = false
  MeasureType = 1
  OverTolerance = 0
  References2D = -> [View]
  Rotation = 0
  ScaleType = 0
  TheoreticalExact = false
  Type = 2
  UnderTolerance = -0.2
  X = 61.7953
  Y = 1.34438
FEATURE [TechDraw::DrawViewDimension] Dimension001
  AngleOverride = false
  Arbitrary = false
  ArbitraryTolerances = false
  EqualTolerance = false
  ExtensionAngle = 0
  FormatSpec = %.2w
  FormatSpecOverTolerance = %+.2w
  FormatSpecUnderTolerance = %+.2w
  Inverted = false
  LineAngle = 0
  LockPosition = false
  MeasureType = 1
  OverTolerance = 0
  References2D = -> [View002]
  Rotation = 0
  ScaleType = 0
  TheoreticalExact = false
  Type = 1
  UnderTolerance = -0.2
  X = -6.41479
  Y = 69.0205
FEATURE [TechDraw::DrawViewBalloon] Balloon
  BubbleShape = 6
  EndType = 6
  EndTypeScale = 1
  KinkLength = 0
  LockPosition = false
  OriginX = 70.4982
  OriginY = 52.3109
  Rotation = 0
  ScaleType = 0
  ShapeScale = 1
  SourceView = -> Dimension
  Text = C
  TextWrapLen = -1
  X = 70.6756
  Y = 62.9547
FEATURE [TechDraw::DrawViewBalloon] Balloon001
  BubbleShape = 6
  EndType = 6
  EndTypeScale = 1
  KinkLength = -0.1
  LockPosition = false
  OriginX = -52.3226
  OriginY = 62.1981
  Rotation = 0
  ScaleType = 0
  ShapeScale = 1
  SourceView = -> Dimension001
  Text = B
  TextWrapLen = -1
  X = -60.7084
  Y = 62.1751
FEATURE [TechDraw::DrawViewBalloon] Balloon002
  BubbleShape = 6
  EndType = 0
  EndTypeScale = 1
  KinkLength = -0.1
  LockPosition = false
  OriginX = 0.5
  OriginY = 0
  Rotation = 0
  ScaleType = 0
  ShapeScale = 1
  SourceView = -> View001
  Text = ⏥|0,2
  TextWrapLen = -1
  X = 19.0698
  Y = 0.107397
FEATURE [TechDraw::DrawViewBalloon] Balloon003
  BubbleShape = 6
  EndType = 6
  EndTypeScale = 1
  KinkLength = -0.1
  LockPosition = false
  OriginX = 0.672888
  OriginY = 39.7383
  Rotation = 0
  ScaleType = 0
  ShapeScale = 1
  SourceView = -> View001
  Text = A
  TextWrapLen = -1
  X = 10.7916
  Y = 39.8457
FEATURE [TechDraw::DrawViewDimension] Dimension003
  AngleOverride = false
  Arbitrary = false
  ArbitraryTolerances = false
  EqualTolerance = true
  ExtensionAngle = 0
  FormatSpec = 2x ⌀%.2w
  FormatSpecOverTolerance = %+.2w
  FormatSpecUnderTolerance = %+.2w
  Inverted = false
  LineAngle = 0
  LockPosition = false
  MeasureType = 1
  OverTolerance = 0
  References2D = -> [View]
  Rotation = 0
  ScaleType = 0
  TheoreticalExact = false
  Type = 0
  UnderTolerance = 0
  X = -11.777
  Y = 72.7869
FEATURE [TechDraw::DrawViewBalloon] Balloon005
  BubbleShape = 6
  EndType = 6
  EndTypeScale = 1
  KinkLength = -0.1
  LockPosition = false
  OriginX = -31.9077
  OriginY = 67.4956
  Rotation = 0
  ScaleType = 0
  ShapeScale = 1
  SourceView = -> Dimension003
  Text = D
  TextWrapLen = -1
  X = -43.255
  Y = 67.5316
FEATURE [TechDraw::DrawViewBalloon] Balloon006
  BubbleShape = 6
  EndType = 7
  EndTypeScale = 1
  KinkLength = 0
  LockPosition = false
  OriginX = -8.73717
  OriginY = 64.838
  Rotation = 0
  ScaleType = 0
  ShapeScale = 1
  SourceView = -> Dimension003
  Text = ⌖|⌀ 0,15|A|B|C
  TextWrapLen = -1
  X = 9.10088
  Y = 61.9493
FEATURE [TechDraw::DrawViewDimension] Dimension004
  AngleOverride = false
  Arbitrary = false
  ArbitraryTolerances = false
  EqualTolerance = true
  ExtensionAngle = 0
  FormatSpec = 2x (⌀%.2w)
  FormatSpecOverTolerance = %+.2w
  FormatSpecUnderTolerance = %+.2w
  Inverted = false
  LineAngle = 0
  LockPosition = false
  MeasureType = 1
  OverTolerance = 0
  References2D = -> [View]
  Rotation = 0
  ScaleType = 0
  TheoreticalExact = false
  Type = 5
  UnderTolerance = 0
  X = 56.2833
  Y = 86.7255
FEATURE [TechDraw::DrawViewBalloon] Balloon007
  BubbleShape = 6
  EndType = 6
  EndTypeScale = 1
  KinkLength = 0
  LockPosition = false
  OriginX = 60.4502
  OriginY = 83.6888
  Rotation = 0
  ScaleType = 0
  ShapeScale = 1
  SourceView = -> Dimension004
  Text = ◎|⌀ 0,15|D
  TextWrapLen = -1
  X = 65.8595
  Y = 75.7457
FEATURE [TechDraw::DrawViewBalloon] Balloon008
  BubbleShape = 1
  EndType = 0
  EndTypeScale = 1
  KinkLength = -0.1
  LockPosition = false
  OriginX = -52.0652
  OriginY = 52.0652
  Rotation = 0
  ScaleType = 0
  ShapeScale = 1
  SourceView = -> View
  Text = 4x R0,38
  TextWrapLen = -1
  X = -75.4388
  Y = 68.3556
FEATURE [TechDraw::DrawViewDimension] Dimension006
  AngleOverride = false
  Arbitrary = false
  ArbitraryTolerances = false
  EqualTolerance = true
  ExtensionAngle = 0
  FormatSpec = 18x ⌀%.2w
  FormatSpecOverTolerance = %+.2w
  FormatSpecUnderTolerance = %+.2w
  Inverted = false
  LineAngle = 0
  LockPosition = false
  MeasureType = 1
  OverTolerance = 0.05
  References2D = -> [View002]
  Rotation = 0
  ScaleType = 0
  TheoreticalExact = false
  Type = 5
  UnderTolerance = -0.05
  X = 78.3293
  Y = -25.4917
FEATURE [TechDraw::DrawViewBalloon] Balloon010
  BubbleShape = 6
  EndType = 6
  EndTypeScale = 1
  KinkLength = 0
  LockPosition = false
  OriginX = 57.3508
  OriginY = -80.6381
  Rotation = 0
  ScaleType = 0
  ShapeScale = 1
  SourceView = -> Dimension006
  Text = ⌖|⌀ 0,15|A|B|C
  TextWrapLen = -1
  X = 91.3024
  Y = -36.3012
FEATURE [TechDraw::DrawComplexSection] ComplexSection  label="Section A - A"
  BaseView = -> View
  Caption = Section A-A
  CoarseView = false
  CutSurfaceDisplay = 2
  CuttingToolWireObject = -> Sketch026
  Direction = (1e-16,-1,0)
  FileGeomPattern = C:/Program Files/FreeCAD 0.21/data/Mod/TechDraw/PAT/FCPAT.pat
  FileHatchPattern = C:/Program Files/FreeCAD 0.21/data/Mod/TechDraw/Patterns/simple.svg
  Focus = 100
  FuseBeforeCut = false
  HardHidden = true
  HatchOffset = (0,0,0)
  HatchRotation = 0
  HatchScale = 1
  IsoCount = 0
  IsoHidden = false
  IsoVisible = false
  LockPosition = false
  NameGeomPattern = Gyémánt bevonatú
  Perspective = false
  ProjectionStrategy = 1
  Rotation = 0
  Scale = 10
  ScaleType = 2
  ScrubCount = 0
  SeamHidden = false
  SeamVisible = true
  SectionDirection = 4
  SectionNormal = (1e-16,-1,0)
  SectionOrigin = (0,0,0)
  SectionSymbol = A
  SmoothHidden = false
  SmoothVisible = true
  Source = -> [Body011]
  TrimAfterCut = false
  X = 89.9827
  XDirection = (1,1e-16,0)
  Y = 81.1022
FEATURE [TechDraw::DrawViewDimension] Dimension007
  AngleOverride = false
  Arbitrary = false
  ArbitraryTolerances = false
  EqualTolerance = true
  ExtensionAngle = 0
  FormatSpec = %.2w
  FormatSpecOverTolerance = %+.2w
  FormatSpecUnderTolerance = %+.2w
  Inverted = false
  LineAngle = 0
  LockPosition = false
  MeasureType = 1
  OverTolerance = 0
  References2D = -> [ComplexSection]
  Rotation = 0
  ScaleType = 0
  TheoreticalExact = false
  Type = 6
  UnderTolerance = 0
  X = -23.1172
  Y = 22.8219
FEATURE [TechDraw::DrawViewDimension] Dimension008
  AngleOverride = false
  Arbitrary = false
  ArbitraryTolerances = false
  EqualTolerance = true
  ExtensionAngle = 0
  FormatSpec = 4x ⌀%.2w
  FormatSpecOverTolerance = %+.2w
  FormatSpecUnderTolerance = %+.2w
  Inverted = false
  LineAngle = 0
  LockPosition = false
  MeasureType = 1
  OverTolerance = 0
  References2D = -> [ComplexSection]
  Rotation = 0
  ScaleType = 0
  TheoreticalExact = false
  Type = 1
  UnderTolerance = 0
  X = 25.5096
  Y = 18.3127
FEATURE [TechDraw::DrawViewDimension] Dimension009
  AngleOverride = false
  Arbitrary = false
  ArbitraryTolerances = false
  EqualTolerance = true
  ExtensionAngle = 0
  FormatSpec = 4x ⌀%.2w
  FormatSpecOverTolerance = %+.2w
  FormatSpecUnderTolerance = %+.2w
  Inverted = false
  LineAngle = 0
  LockPosition = false
  MeasureType = 1
  OverTolerance = 0.05
  References2D = -> [ComplexSection]
  Rotation = 0
  ScaleType = 0
  TheoreticalExact = false
  Type = 1
  UnderTolerance = -0.05
  X = 48.7908
  Y = -4.80347
FEATURE [TechDraw::DrawViewBalloon] Balloon012
  BubbleShape = 6
  EndType = 6
  EndTypeScale = 1
  KinkLength = 0
  LockPosition = false
  OriginX = 46.1954
  OriginY = -17.0078
  Rotation = 0
  ScaleType = 0
  ShapeScale = 1
  SourceView = -> Dimension009
  Text = ⌖|⌀ 0,15|A|B|C
  TextWrapLen = -1
  X = 60.7039
  Y = -15.6117
FEATURE [TechDraw::DrawViewDimension] Dimension010
  AngleOverride = false
  Arbitrary = false
  ArbitraryTolerances = false
  EqualTolerance = true
  ExtensionAngle = 0
  FormatSpec = (%.2w)
  FormatSpecOverTolerance = %+.2w
  FormatSpecUnderTolerance = %+.2w
  Inverted = false
  LineAngle = 0
  LockPosition = false
  MeasureType = 1
  OverTolerance = 0
  References2D = -> [ComplexSection]
  Rotation = 0
  ScaleType = 0
  TheoreticalExact = false
  Type = 2
  UnderTolerance = 0
  X = -36.693
  Y = 2
FEATURE [TechDraw::DrawViewAnnotation] Annotation
  Font = osifont
  LineSpace = 100
  LockPosition = false
  MaxWidth = -1
  Rotation = 0
  ScaleType = 0
  Text = 10:1
  TextSize = 4
  TextStyle = 0
  X = 86.742
  Y = 60.6655
FEATURE [TechDraw::DrawViewPart] View003
  CoarseView = false
  Direction = (0.57735,0.57735,0.57735)
  Focus = 100
  HardHidden = true
  IsoCount = 0
  IsoHidden = false
  IsoVisible = false
  LockPosition = false
  Perspective = false
  Rotation = 0
  Scale = 0.5
  ScaleType = 2
  ScrubCount = 0
  SeamHidden = false
  SeamVisible = true
  SmoothHidden = false
  SmoothVisible = true
  Source = -> [Body011]
  X = 386.287
  XDirection = (0.707107,0,-0.707107)
  Y = 119.321
FEATURE [TechDraw::DrawHatch] Hatch  label="HatchF1"
  HatchPattern = C:/Program Files/FreeCAD 0.21/data/Mod/TechDraw/Patterns/solid.svg
  Source = -> View003 [Face1]
FEATURE [TechDraw::DrawViewBalloon] Balloon013
  BubbleShape = 1
  EndType = 3
  EndTypeScale = 1
  KinkLength = -0.1
  LockPosition = false
  OriginX = -18.2151
  OriginY = -14.1288
  Rotation = 0
  ScaleType = 0
  ShapeScale = 1
  SourceView = -> View003
  TextWrapLen = -1
  X = -113.902
  Y = -52.9975
FEATURE [TechDraw::DrawViewAnnotation] Annotation001
  Font = osifont
  LineSpace = 100
  LockPosition = false
  MaxWidth = -1
  Rotation = 0
  ScaleType = 0
  Text = 1:2
  TextSize = 4
  TextStyle = 0
  X = 381.918
  Y = 90.0973
FEATURE [TechDraw::DrawViewAnnotation] Annotation002
  Font = osifont
  LineSpace = 100
  LockPosition = false
  MaxWidth = -1
  Rotation = 0
  ScaleType = 0
  Text = The mid of the datum plane A is preferred to be near | to the lower limit of the flatness tolerance zone. | It can be achieved with an additional bending step. | Aesthetical surfaces colored red on the view | No scratches, burrs or any kind of damage allowed! | Functional surfaces colored blue on the view (all which perpendicular to the aesthetical) | No burrs or other protruding material allowed!
  TextSize = 3
  TextStyle = 0
  X = 295.979
  Y = 101.86
FEATURE [TechDraw::DrawViewBalloon] Balloon015
  BubbleShape = 2
  EndType = 6
  EndTypeScale = 1
  KinkLength = 0
  LockPosition = false
  OriginX = -87.396
  OriginY = 27.2009
  Rotation = 0
  ScaleType = 0
  ShapeScale = 1
  SourceView = -> Annotation002
  Text = 3
  TextWrapLen = -1
  X = -96.2531
  Y = -1.91575
FEATURE [TechDraw::DrawViewDimension] Dimension011
  AngleOverride = false
  Arbitrary = false
  ArbitraryTolerances = false
  EqualTolerance = true
  ExtensionAngle = 0
  FormatSpec = 8× ⌀%.2w
  FormatSpecOverTolerance = %+.2w
  FormatSpecUnderTolerance = %+.2w
  Inverted = false
  LineAngle = 0
  LockPosition = false
  MeasureType = 1
  OverTolerance = 0
  References2D = -> [View002]
  Rotation = 0
  ScaleType = 0
  TheoreticalExact = false
  Type = 5
  UnderTolerance = 0
  X = 75.2192
  Y = -60.9974
FEATURE [TechDraw::DrawViewDimension] Dimension012
  AngleOverride = false
  Arbitrary = false
  ArbitraryTolerances = true
  EqualTolerance = false
  ExtensionAngle = 0
  FormatSpec = 8× ⌀%.2w
  FormatSpecOverTolerance = +0,15
  FormatSpecUnderTolerance = 0
  Inverted = false
  LineAngle = 0
  LockPosition = false
  MeasureType = 1
  OverTolerance = 0
  References2D = -> [View002]
  Rotation = 0
  ScaleType = 0
  TheoreticalExact = false
  Type = 5
  UnderTolerance = 0
  X = 72.4963
  Y = 8.04101
FEATURE [TechDraw::DrawViewBalloon] Balloon016
  BubbleShape = 6
  EndType = 6
  EndTypeScale = 1
  KinkLength = 0
  LockPosition = false
  OriginX = 79.0426
  OriginY = -7.7627
  Rotation = 0
  ScaleType = 0
  ShapeScale = 1
  SourceView = -> Dimension012
  Text = ⌖|⌀ 0,15|A|B|C
  TextWrapLen = -1
  X = 92.0678
  Y = -4.70292
FEATURE [TechDraw::DrawViewBalloon] Balloon017
  BubbleShape = 6
  EndType = 6
  EndTypeScale = 1
  KinkLength = 0
  LockPosition = false
  OriginX = 75.1018
  OriginY = -15.0221
  Rotation = 0
  ScaleType = 0
  ShapeScale = 1
  SourceView = -> Dimension012
  Text = ○|0,1
  TextWrapLen = -1
  X = 73.0244
  Y = -15.3225
FEATURE [TechDraw::DrawViewBalloon] Balloon018
  BubbleShape = 2
  EndType = 6
  EndTypeScale = 1
  KinkLength = 0
  LockPosition = false
  OriginX = 84.1342
  OriginY = 3.44725
  Rotation = 0
  ScaleType = 0
  ShapeScale = 1
  SourceView = -> Dimension012
  Text = 3
  TextWrapLen = -1
  X = 101.675
  Y = 5.46919
FEATURE [TechDraw::DrawViewBalloon] Balloon019
  BubbleShape = 1
  EndType = 0
  EndTypeScale = 1
  KinkLength = 0
  LockPosition = false
  OriginX = 0.785937
  OriginY = -33.6238
  Rotation = 0
  ScaleType = 0
  ShapeScale = 1
  SourceView = -> View001
  TextWrapLen = -1
  X = 22.117
  Y = -64.3933
FEATURE [TechDraw::DrawPage] Page  label="TEK2_Drawing"
  KeepUpdated = true
  NextBalloonIndex = 21
  ProjectionType = 0
  Template = -> Template
  Views = -> [View,View001,View002,Dimension,Dimension001,Balloon,Balloon001,Balloon002,Balloon003,Dimension003,Balloon005,Balloon006,Dimension004,Balloon007,Balloon008,Dimension006,Balloon010,ComplexSection,Dimension007,Dimension008,Dimension009,Balloon012,Dimension010,Annotation,View003,Balloon013,Annotation001,Annotation002,Balloon015,Dimension011,Dimension012,Balloon016,Balloon017,Balloon018,Balloon019]
FEATURE [TechDraw::DrawSVGTemplate] Template001
  Height = 210
  Orientation = 1
  Template = C:/Program Files/FreeCAD 0.21/data/Mod/TechDraw/Templates/A4_Landscape_blank.svg
  Width = 297
FEATURE [TechDraw::DrawViewPart] View004
  CoarseView = false
  Direction = (0,0,1)
  Focus = 100
  HardHidden = false
  IsoCount = 0
  IsoHidden = false
  IsoVisible = true
  LockPosition = false
  Perspective = false
  Rotation = 0
  ScaleType = 0
  ScrubCount = 0
  SeamHidden = false
  SeamVisible = true
  SmoothHidden = false
  SmoothVisible = true
  Source = -> [Body011]
  X = 148.5
  XDirection = (1,1e-06,0)
  Y = 105
FEATURE [TechDraw::DrawPage] Page001  label="TEK2_dxf"
  KeepUpdated = true
  NextBalloonIndex = 1
  ProjectionType = 0
  Template = -> Template001
  Views = -> [View004]
FEATURE [TechDraw::DrawHatch] Hatch004  label="Hatch004F56"
  HatchPattern = C:/Program Files/FreeCAD 0.21/data/Mod/TechDraw/Patterns/solid.svg
  Source = -> View003 [Face56,Face3,Face61,Face74,Face75,Face60,Face76]
FEATURE [TechDraw::DrawHatch] Hatch005  label="Hatch005F65"
  HatchPattern = C:/Program Files/FreeCAD 0.21/data/Mod/TechDraw/Patterns/solid.svg
  Source = -> View003 [Face65,Face62,Face72,Face64,Face69,Face59,Face2,Face100]
FEATURE [TechDraw::DrawHatch] Hatch006  label="Hatch006F24"
  HatchPattern = C:/Program Files/FreeCAD 0.21/data/Mod/TechDraw/Patterns/solid.svg
  Source = -> View003 [Face24,Face25,Face57,Face58]
FEATURE [TechDraw::DrawHatch] Hatch007  label="Hatch007F31"
  HatchPattern = C:/Program Files/FreeCAD 0.21/data/Mod/TechDraw/Patterns/solid.svg
  Source = -> View003 [Face31,Face63,Face66,Face30,Face68,Face29,Face32,Face73,Face67,Face27,Face71,Face28,Face70,Face33,Face77,Face26]
